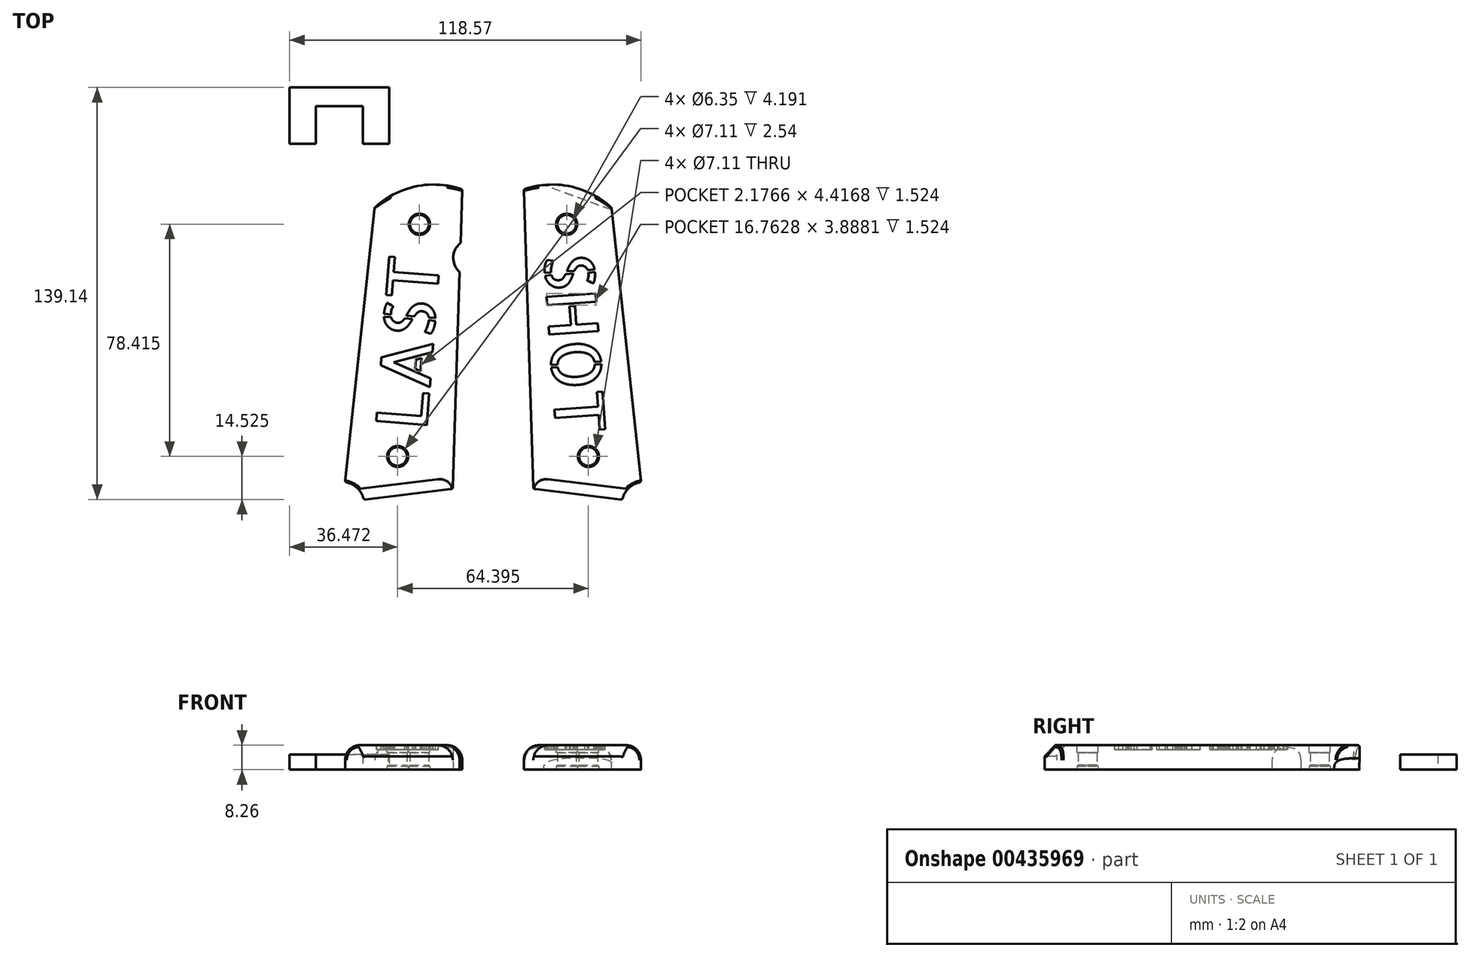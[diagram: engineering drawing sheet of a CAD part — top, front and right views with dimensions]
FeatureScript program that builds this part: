
annotation { "Feature Type Name" : "Feature", "Feature Type Description" : "" }
export const myFeature = defineFeature(function(context is Context, id is Id, definition is map)
    precondition{}
    {
        {
            var Q0;
            Q0=qCreatedBy(makeId("Top.planeOp"),FACE);
            var sketch = newSketch(context, id + "F0", { "sketchPlane" : qUnion([Q0])});
            skLineSegment(sketch, "E0", {"start": v(-13.61, -63.5) * mm, "end": v(-43.66, -67.13) * mm});
            skArc(sketch, "E1", {"start": v(-10.4, 37.63) * mm, "mid": v(-26.05, 38.66) * mm, "end": v(-39.98, 31.44) * mm});
            skArc(sketch, "E2", {"start": v(-10.97, 19.52) * mm, "mid": v(-13.43, 14.7) * mm, "end": v(-11.28, 9.73) * mm});
            skLineSegment(sketch, "E3", {"start": v(-10.4, 37.63) * mm, "end": v(-10.97, 19.52) * mm});
            skLineSegment(sketch, "E4", {"start": v(-11.28, 9.73) * mm, "end": v(-13.61, -63.5) * mm});
            skCircle(sketch, "E5", {"center": v(-32.2, -52.55) * mm, "radius": 3.18 * mm});
            skCircle(sketch, "E6", {"center": v(-24.84, 25.87) * mm, "radius": 3.18 * mm});
            skArc(sketch, "E7", {"start": v(-43.66, -67.13) * mm, "mid": v(-45.85, -63.16) * mm, "end": v(-49.96, -61.24) * mm});
            skLineSegment(sketch, "E8.trimOffspring", {"start": v(-49.96, -61.24) * mm, "end": v(-39.98, 31.44) * mm});
            skPoint(sketch, "E9.orphan", {"position": v(-51.52, -68.08) * mm});
            skPoint(sketch, "E10.MirrorP", {"position": v(51.52, -68.08) * mm});
            skCircle(sketch, "E11.MirrorC", {"center": v(24.84, 25.87) * mm, "radius": 3.18 * mm});
            skCircle(sketch, "E12.MirrorC", {"center": v(32.2, -52.55) * mm, "radius": 3.18 * mm});
            skLineSegment(sketch, "E13.MirrorCS", {"start": v(11.28, 9.73) * mm, "end": v(13.61, -63.5) * mm});
            skLineSegment(sketch, "E14.MirrorCS", {"start": v(10.4, 37.63) * mm, "end": v(10.97, 19.52) * mm});
            skLineSegment(sketch, "E15.MirrorCS", {"start": v(49.96, -61.24) * mm, "end": v(39.98, 31.44) * mm});
            skArc(sketch, "E16.MirrorCS", {"start": v(43.66, -67.13) * mm, "mid": v(45.85, -63.16) * mm, "end": v(49.96, -61.24) * mm});
            skLineSegment(sketch, "E17.MirrorCS", {"start": v(13.61, -63.5) * mm, "end": v(43.66, -67.13) * mm});
            skArc(sketch, "E18.MirrorCS", {"start": v(10.4, 37.63) * mm, "mid": v(26.05, 38.66) * mm, "end": v(39.98, 31.44) * mm});
            skLineSegment(sketch, "E19", {"start": v(10.97, 19.52) * mm, "end": v(11.28, 9.73) * mm});
            skSolve(sketch);
        }
        {
            var Q0;
            Q0 = qSketchRegion(id + "F0", true);
            extrude(context, id + "F1", {"entities" : qUnion([Q0]), "depth" : 8.25 * mm});
        }
        {
            var Q0;
            Q0=qCreatedBy(makeId("Top.planeOp"),FACE);
            var sketch = newSketch(context, id + "F2", { "sketchPlane" : qUnion([Q0])});
            skLineSegment(sketch, "E20", {"start": v(-59.78, 65.72) * mm, "end": v(-43.9, 65.72) * mm});
            skLineSegment(sketch, "E21", {"start": v(-43.9, 65.72) * mm, "end": v(-43.9, 53.02) * mm});
            skLineSegment(sketch, "E22", {"start": v(-43.9, 53.02) * mm, "end": v(-35.01, 53.02) * mm});
            skLineSegment(sketch, "E23", {"start": v(-35.01, 53.02) * mm, "end": v(-35.01, 72.07) * mm});
            skLineSegment(sketch, "E24", {"start": v(-35.01, 72.07) * mm, "end": v(-68.67, 72.07) * mm});
            skLineSegment(sketch, "E25", {"start": v(-68.67, 72.07) * mm, "end": v(-68.67, 53.02) * mm});
            skLineSegment(sketch, "E26", {"start": v(-68.67, 53.02) * mm, "end": v(-59.78, 53.02) * mm});
            skLineSegment(sketch, "E27", {"start": v(-59.78, 53.02) * mm, "end": v(-59.78, 65.72) * mm});
            skSolve(sketch);
        }
        {
            var Q0;
            Q0 = qSketchRegion(id + "F2", true);
            extrude(context, id + "F3", {"entities" : qUnion([Q0]), "depth" : 5.08 * mm});
        }
        {
            var Q0;
            Q0=qCreatedBy(makeId("Front.planeOp"),FACE);
            var sketch = newSketch(context, id + "F4", { "sketchPlane" : qUnion([Q0])});
            skLineSegment(sketch, "E28", {"start": v(0, 75.66) * mm, "end": v(0, -56.7) * mm});
            skSolve(sketch);
        }
        {
            var Q0;
            Q0=sQuery(id+"F4.wireOp",EDGE,"E28");
            cPlane(context, id + "F5", {"entities" : qUnion([Q0]), "cplaneType" : CPlaneType.LINE_ANGLE, "offset" : 25.4 * mm, "angle" : 20 * degree, "width" : 152.4 * mm, "height" : 152.4 * mm});
        }
        {
            var Q0;
            Q0=qCreatedBy(id+"F5.planeOp",FACE);
            var sketch = newSketch(context, id + "F6", { "sketchPlane" : qUnion([Q0])});
            skCircle(sketch, "E29", {"center": v(-45.72, 0.67) * mm, "radius": 3.18 * mm});
            skSolve(sketch);
        }
        {
            var Q0;
            Q0 = qSketchRegion(id + "F6", true);
            extrude(context, id + "F7", {"entities" : qUnion([Q0]), "operationType" : NewBodyOperationType.REMOVE, "oppositeDirection" : true, "depth" : 38.1 * mm});
        }
        {
            var Q0;
            Q0=makeQuery(id+"F1.opExtrude","CAP_EDGE",EDGE,{"disambiguationData":[OSD([sQuery(id+"F0.wireOp",EDGE,"a4e4d398-114f-4659-ac55-d26a9042ed512.MirrorCS")])],"isStart":false});
            var Q1;
            Q1=makeQuery(id+"F1.opExtrude","CAP_EDGE",EDGE,{"disambiguationData":[OSD([sQuery(id+"F0.wireOp",EDGE,"fEtNWjUg-NbEW-A6zS-67Gl-Nols5Lw7AtEy")])],"isStart":false});
            var Q2;
            Q2=makeQuery(id+"F1.opExtrude","CAP_EDGE",EDGE,{"disambiguationData":[OSD([sQuery(id+"F0.wireOp",EDGE,"E4")])],"isStart":false});
            var Q3;
            Q3=makeQuery(id+"F1.opExtrude","CAP_EDGE",EDGE,{"disambiguationData":[OSD([sQuery(id+"F0.wireOp",EDGE,"a4e4d398-114f-4659-ac55-d26a9042ed510.MirrorCS")])],"isStart":false});
            fillet(context, id + "F8", {"entities" : qUnion([Q0, Q1, Q2, Q3]), "radius" : 5.08 * mm, "tangentPropagation" : true, "allowEdgeOverflow" : false});
        }
        {
            var Q0;
            Q0=makeQuery(id+"F1.opExtrude","CAP_EDGE",EDGE,{"disambiguationData":[OSD([sQuery(id+"F0.wireOp",EDGE,"E13.MirrorCS"),sQuery(id+"F0.wireOp",EDGE,"E14.MirrorCS"),sQuery(id+"F0.wireOp",EDGE,"E19")])],"isStart":false});
            var Q1;
            Q1=makeQuery(id+"F1.opExtrude","CAP_EDGE",EDGE,{"disambiguationData":[OSD([sQuery(id+"F0.wireOp",EDGE,"E15.MirrorCS")])],"isStart":false});
            var Q2;
            Q2=makeQuery(id+"F1.opExtrude","CAP_EDGE",EDGE,{"disambiguationData":[OSD([sQuery(id+"F0.wireOp",EDGE,"E8.trimOffspring")])],"isStart":false});
            fillet(context, id + "F9", {"entities" : qUnion([Q0, Q1, Q2]), "radius" : 5.08 * mm, "tangentPropagation" : true, "allowEdgeOverflow" : false});
        }
        {
            var Q0;
            Q0=makeQuery(id+"F1.opExtrude","CAP_EDGE",EDGE,{"disambiguationData":[OSD([sQuery(id+"F0.wireOp",EDGE,"E0")])],"isStart":false});
            var Q1;
            Q1=makeQuery(id+"F1.opExtrude","CAP_EDGE",EDGE,{"disambiguationData":[OSD([sQuery(id+"F0.wireOp",EDGE,"E17.MirrorCS")])],"isStart":false});
            chamfer(context, id + "F10", {"entities" : qUnion([Q0, Q1]), "width" : 3.8 * mm});
        }
        {
            var Q0;
            Q0=makeQuery(id+"F1.opExtrude","CAP_EDGE",EDGE,{"disambiguationData":[OSD([sQuery(id+"F0.wireOp",EDGE,"E18.MirrorCS")])],"isStart":false});
            var Q1;
            Q1=makeQuery(id+"F9.opFillet","BLEND_EDGE",EDGE,{"blendedFrom":[makeQuery(id+"F1.opExtrude","CAP_EDGE",EDGE,{"disambiguationData":[OSD([sQuery(id+"F0.wireOp",EDGE,"E13.MirrorCS"),sQuery(id+"F0.wireOp",EDGE,"E14.MirrorCS"),sQuery(id+"F0.wireOp",EDGE,"E19")])],"isStart":false}),makeQuery(id+"F1.opExtrude","SWEPT_FACE",FACE,{"disambiguationData":[OSD([sQuery(id+"F0.wireOp",EDGE,"E18.MirrorCS")])]})],"blendedInto":[makeQuery(id+"F1.opExtrude","SWEPT_FACE",FACE,{"disambiguationData":[OSD([sQuery(id+"F0.wireOp",EDGE,"E18.MirrorCS")])]})]});
            var Q2;
            Q2=makeQuery(id+"F1.opExtrude","SWEPT_EDGE",EDGE,{"disambiguationData":[OSD([sQuery(id+"F0.wireOp",EDGE,"E14.MirrorCS"),sQuery(id+"F0.wireOp",EDGE,"E18.MirrorCS")])]});
            var Q3;
            Q3=makeQuery(id+"F9.opFillet","BLEND_EDGE",EDGE,{"blendedFrom":[makeQuery(id+"F1.opExtrude","CAP_EDGE",EDGE,{"disambiguationData":[OSD([sQuery(id+"F0.wireOp",EDGE,"E15.MirrorCS")])],"isStart":false}),makeQuery(id+"F1.opExtrude","SWEPT_FACE",FACE,{"disambiguationData":[OSD([sQuery(id+"F0.wireOp",EDGE,"E18.MirrorCS")])]})],"blendedInto":[makeQuery(id+"F1.opExtrude","SWEPT_FACE",FACE,{"disambiguationData":[OSD([sQuery(id+"F0.wireOp",EDGE,"E18.MirrorCS")])]})]});
            var Q4;
            Q4=makeQuery(id+"F1.opExtrude","SWEPT_EDGE",EDGE,{"disambiguationData":[OSD([sQuery(id+"F0.wireOp",EDGE,"E1"),sQuery(id+"F0.wireOp",EDGE,"E3")])]});
            var Q5;
            Q5=makeQuery(id+"F8.opFillet","BLEND_EDGE",EDGE,{"blendedFrom":[makeQuery(id+"F1.opExtrude","CAP_EDGE",EDGE,{"disambiguationData":[OSD([sQuery(id+"F0.wireOp",EDGE,"E4")])],"isStart":false}),makeQuery(id+"F1.opExtrude","SWEPT_FACE",FACE,{"disambiguationData":[OSD([sQuery(id+"F0.wireOp",EDGE,"E1")])]})],"blendedInto":[makeQuery(id+"F1.opExtrude","SWEPT_FACE",FACE,{"disambiguationData":[OSD([sQuery(id+"F0.wireOp",EDGE,"E1")])]})]});
            var Q6;
            Q6=makeQuery(id+"F1.opExtrude","CAP_EDGE",EDGE,{"disambiguationData":[OSD([sQuery(id+"F0.wireOp",EDGE,"E1")])],"isStart":false});
            var Q7;
            Q7=makeQuery(id+"F9.opFillet","BLEND_EDGE",EDGE,{"blendedFrom":[makeQuery(id+"F1.opExtrude","CAP_EDGE",EDGE,{"disambiguationData":[OSD([sQuery(id+"F0.wireOp",EDGE,"E8.trimOffspring")])],"isStart":false}),makeQuery(id+"F1.opExtrude","SWEPT_FACE",FACE,{"disambiguationData":[OSD([sQuery(id+"F0.wireOp",EDGE,"E1")])]})],"blendedInto":[makeQuery(id+"F1.opExtrude","SWEPT_FACE",FACE,{"disambiguationData":[OSD([sQuery(id+"F0.wireOp",EDGE,"E1")])]})]});
            var Q8;
            Q8=makeQuery(id+"F1.opExtrude","SWEPT_EDGE",EDGE,{"disambiguationData":[OSD([sQuery(id+"F0.wireOp",EDGE,"E0"),sQuery(id+"F0.wireOp",EDGE,"E4")])]});
            var Q9;
            Q9=makeQuery(id+"F8.opFillet","BLEND_EDGE",EDGE,{"blendedFrom":[makeQuery(id+"F1.opExtrude","CAP_EDGE",EDGE,{"disambiguationData":[OSD([sQuery(id+"F0.wireOp",EDGE,"E4")])],"isStart":false}),makeQuery(id+"F1.opExtrude","SWEPT_FACE",FACE,{"disambiguationData":[OSD([sQuery(id+"F0.wireOp",EDGE,"E0")])]})],"blendedInto":[makeQuery(id+"F1.opExtrude","SWEPT_FACE",FACE,{"disambiguationData":[OSD([sQuery(id+"F0.wireOp",EDGE,"E0")])]})]});
            var Q10;
            Q10=makeQuery(id+"F1.opExtrude","SWEPT_EDGE",EDGE,{"disambiguationData":[OSD([sQuery(id+"F0.wireOp",EDGE,"E0"),sQuery(id+"F0.wireOp",EDGE,"E7")])]});
            var Q11;
            Q11=makeQuery(id+"F10.opChamfer","BLEND_EDGE",EDGE,{"blendedFrom":[makeQuery(id+"F1.opExtrude","CAP_EDGE",EDGE,{"disambiguationData":[OSD([sQuery(id+"F0.wireOp",EDGE,"E0")])],"isStart":false}),makeQuery(id+"F1.opExtrude","SWEPT_FACE",FACE,{"disambiguationData":[OSD([sQuery(id+"F0.wireOp",EDGE,"E7")])]})],"blendedInto":[makeQuery(id+"F1.opExtrude","SWEPT_FACE",FACE,{"disambiguationData":[OSD([sQuery(id+"F0.wireOp",EDGE,"E7")])]})]});
            var Q12;
            Q12=makeQuery(id+"F1.opExtrude","SWEPT_EDGE",EDGE,{"disambiguationData":[OSD([sQuery(id+"F0.wireOp",EDGE,"E7"),sQuery(id+"F0.wireOp",EDGE,"E8.trimOffspring")])]});
            var Q13;
            Q13=makeQuery(id+"F9.opFillet","BLEND_EDGE",EDGE,{"blendedFrom":[makeQuery(id+"F1.opExtrude","CAP_EDGE",EDGE,{"disambiguationData":[OSD([sQuery(id+"F0.wireOp",EDGE,"E8.trimOffspring")])],"isStart":false}),makeQuery(id+"F1.opExtrude","SWEPT_FACE",FACE,{"disambiguationData":[OSD([sQuery(id+"F0.wireOp",EDGE,"E7")])]})],"blendedInto":[makeQuery(id+"F1.opExtrude","SWEPT_FACE",FACE,{"disambiguationData":[OSD([sQuery(id+"F0.wireOp",EDGE,"E7")])]})]});
            var Q14;
            Q14=makeQuery(id+"F1.opExtrude","CAP_EDGE",EDGE,{"disambiguationData":[OSD([sQuery(id+"F0.wireOp",EDGE,"E7")])],"isStart":false});
            var Q15;
            Q15=makeQuery(id+"F1.opExtrude","SWEPT_EDGE",EDGE,{"disambiguationData":[OSD([sQuery(id+"F0.wireOp",EDGE,"E13.MirrorCS"),sQuery(id+"F0.wireOp",EDGE,"E17.MirrorCS")])]});
            var Q16;
            Q16=makeQuery(id+"F9.opFillet","BLEND_EDGE",EDGE,{"blendedFrom":[makeQuery(id+"F1.opExtrude","CAP_EDGE",EDGE,{"disambiguationData":[OSD([sQuery(id+"F0.wireOp",EDGE,"E13.MirrorCS"),sQuery(id+"F0.wireOp",EDGE,"E14.MirrorCS"),sQuery(id+"F0.wireOp",EDGE,"E19")])],"isStart":false}),makeQuery(id+"F1.opExtrude","SWEPT_FACE",FACE,{"disambiguationData":[OSD([sQuery(id+"F0.wireOp",EDGE,"E17.MirrorCS")])]})],"blendedInto":[makeQuery(id+"F1.opExtrude","SWEPT_FACE",FACE,{"disambiguationData":[OSD([sQuery(id+"F0.wireOp",EDGE,"E17.MirrorCS")])]})]});
            var Q17;
            Q17=makeQuery(id+"F1.opExtrude","SWEPT_EDGE",EDGE,{"disambiguationData":[OSD([sQuery(id+"F0.wireOp",EDGE,"E16.MirrorCS"),sQuery(id+"F0.wireOp",EDGE,"E17.MirrorCS")])]});
            var Q18;
            Q18=makeQuery(id+"F10.opChamfer","BLEND_EDGE",EDGE,{"blendedFrom":[makeQuery(id+"F1.opExtrude","CAP_EDGE",EDGE,{"disambiguationData":[OSD([sQuery(id+"F0.wireOp",EDGE,"E17.MirrorCS")])],"isStart":false}),makeQuery(id+"F1.opExtrude","SWEPT_FACE",FACE,{"disambiguationData":[OSD([sQuery(id+"F0.wireOp",EDGE,"E16.MirrorCS")])]})],"blendedInto":[makeQuery(id+"F1.opExtrude","SWEPT_FACE",FACE,{"disambiguationData":[OSD([sQuery(id+"F0.wireOp",EDGE,"E16.MirrorCS")])]})]});
            var Q19;
            Q19=makeQuery(id+"F1.opExtrude","CAP_EDGE",EDGE,{"disambiguationData":[OSD([sQuery(id+"F0.wireOp",EDGE,"E16.MirrorCS")])],"isStart":false});
            var Q20;
            Q20=makeQuery(id+"F9.opFillet","BLEND_EDGE",EDGE,{"blendedFrom":[makeQuery(id+"F1.opExtrude","CAP_EDGE",EDGE,{"disambiguationData":[OSD([sQuery(id+"F0.wireOp",EDGE,"E15.MirrorCS")])],"isStart":false}),makeQuery(id+"F1.opExtrude","SWEPT_FACE",FACE,{"disambiguationData":[OSD([sQuery(id+"F0.wireOp",EDGE,"E16.MirrorCS")])]})],"blendedInto":[makeQuery(id+"F1.opExtrude","SWEPT_FACE",FACE,{"disambiguationData":[OSD([sQuery(id+"F0.wireOp",EDGE,"E16.MirrorCS")])]})]});
            var Q21;
            Q21=makeQuery(id+"F1.opExtrude","SWEPT_EDGE",EDGE,{"disambiguationData":[OSD([sQuery(id+"F0.wireOp",EDGE,"E15.MirrorCS"),sQuery(id+"F0.wireOp",EDGE,"E16.MirrorCS")])]});
            var Q22;
            Q22=makeQuery(id+"F1.opExtrude","SWEPT_EDGE",EDGE,{"disambiguationData":[OSD([sQuery(id+"F0.wireOp",EDGE,"E1"),sQuery(id+"F0.wireOp",EDGE,"E8.trimOffspring")])]});
            fillet(context, id + "F11", {"entities" : qUnion([Q0, Q1, Q2, Q3, Q4, Q5, Q6, Q7, Q8, Q9, Q10, Q11, Q12, Q13, Q14, Q15, Q16, Q17, Q18, Q19, Q20, Q21, Q22]), "radius" : 0.64 * mm, "tangentPropagation" : true, "allowEdgeOverflow" : false});
        }
        {
            var Q0;
            Q0=makeQuery(id+"F1.opExtrude","CAP_FACE",FACE,{"disambiguationData":[OSD([sQuery(id+"F0.wireOp",EDGE,"E11.MirrorC"),sQuery(id+"F0.wireOp",EDGE,"E12.MirrorC"),sQuery(id+"F0.wireOp",EDGE,"E13.MirrorCS"),sQuery(id+"F0.wireOp",EDGE,"E14.MirrorCS"),sQuery(id+"F0.wireOp",EDGE,"E15.MirrorCS"),sQuery(id+"F0.wireOp",EDGE,"E16.MirrorCS"),sQuery(id+"F0.wireOp",EDGE,"E17.MirrorCS"),sQuery(id+"F0.wireOp",EDGE,"E18.MirrorCS"),sQuery(id+"F0.wireOp",EDGE,"E19")])],"isStart":false});
            var sketch = newSketch(context, id + "F12", { "sketchPlane" : qUnion([Q0])});
            skText(sketch, "E30", { "text": "SHOT", "fontName": "AllertaStencil-Regular.ttf"});
            const initialGuessF12  = {"E30": [0.01709, 0.0156, 0.069, -0.99762, 0.01662]};
            skSetInitialGuess(sketch, initialGuessF12);
            skSolve(sketch);
        }
        {
            var Q0;
            Q0 = qSketchRegion(id + "F12", true);
            extrude(context, id + "F13", {"entities" : qUnion([Q0]), "operationType" : NewBodyOperationType.REMOVE, "oppositeDirection" : true, "depth" : 1.52 * mm});
        }
        {
            var Q0;
            Q0=makeQuery(id+"F1.opExtrude","CAP_FACE",FACE,{"disambiguationData":[OSD([sQuery(id+"F0.wireOp",EDGE,"E0"),sQuery(id+"F0.wireOp",EDGE,"E1"),sQuery(id+"F0.wireOp",EDGE,"E2"),sQuery(id+"F0.wireOp",EDGE,"E3"),sQuery(id+"F0.wireOp",EDGE,"E4"),sQuery(id+"F0.wireOp",EDGE,"E5"),sQuery(id+"F0.wireOp",EDGE,"E6"),sQuery(id+"F0.wireOp",EDGE,"E7"),sQuery(id+"F0.wireOp",EDGE,"E8.trimOffspring")])],"isStart":false});
            var sketch = newSketch(context, id + "F14", { "sketchPlane" : qUnion([Q0])});
            skText(sketch, "E31", { "text": "LAST", "fontName": "AllertaStencil-Regular.ttf"});
            const initialGuessF14  = {"E31": [-0.02256, -0.0441, 0.07965, 0.99682, 0.0171]};
            skSetInitialGuess(sketch, initialGuessF14);
            skSolve(sketch);
        }
        {
            var Q0;
            Q0 = qSketchRegion(id + "F14", true);
            extrude(context, id + "F15", {"entities" : qUnion([Q0]), "operationType" : NewBodyOperationType.REMOVE, "oppositeDirection" : true, "depth" : 1.52 * mm});
        }
        {
            var Q0;
            Q0=makeQuery(id+"F1.opExtrude","CAP_FACE",FACE,{"disambiguationData":[OSD([sQuery(id+"F0.wireOp",EDGE,"E11.MirrorC"),sQuery(id+"F0.wireOp",EDGE,"E12.MirrorC"),sQuery(id+"F0.wireOp",EDGE,"E13.MirrorCS"),sQuery(id+"F0.wireOp",EDGE,"E14.MirrorCS"),sQuery(id+"F0.wireOp",EDGE,"E15.MirrorCS"),sQuery(id+"F0.wireOp",EDGE,"E16.MirrorCS"),sQuery(id+"F0.wireOp",EDGE,"E17.MirrorCS"),sQuery(id+"F0.wireOp",EDGE,"E18.MirrorCS"),sQuery(id+"F0.wireOp",EDGE,"E19")])],"isStart":false});
            var sketch = newSketch(context, id + "F16", { "sketchPlane" : qUnion([Q0])});
            skCircle(sketch, "E32", {"center": v(24.84, 25.87) * mm, "radius": 3.56 * mm});
            skCircle(sketch, "E33", {"center": v(32.2, -52.55) * mm, "radius": 3.56 * mm});
            skSolve(sketch);
        }
        {
            var Q0;
            Q0 = qSketchRegion(id + "F16", true);
            extrude(context, id + "F17", {"entities" : qUnion([Q0]), "operationType" : NewBodyOperationType.REMOVE, "oppositeDirection" : true, "depth" : 2.54 * mm});
        }
        {
            var Q0;
            Q0=makeQuery(id+"F1.opExtrude","CAP_FACE",FACE,{"disambiguationData":[OSD([sQuery(id+"F0.wireOp",EDGE,"E0"),sQuery(id+"F0.wireOp",EDGE,"E1"),sQuery(id+"F0.wireOp",EDGE,"E2"),sQuery(id+"F0.wireOp",EDGE,"E3"),sQuery(id+"F0.wireOp",EDGE,"E4"),sQuery(id+"F0.wireOp",EDGE,"E5"),sQuery(id+"F0.wireOp",EDGE,"E6"),sQuery(id+"F0.wireOp",EDGE,"E7"),sQuery(id+"F0.wireOp",EDGE,"E8.trimOffspring")])],"isStart":false});
            var sketch = newSketch(context, id + "F18", { "sketchPlane" : qUnion([Q0])});
            skCircle(sketch, "E34", {"center": v(-24.84, 25.87) * mm, "radius": 3.56 * mm});
            skCircle(sketch, "E35", {"center": v(-32.2, -52.55) * mm, "radius": 3.56 * mm});
            skSolve(sketch);
        }
        {
            var Q0;
            Q0 = qSketchRegion(id + "F18", true);
            extrude(context, id + "F19", {"entities" : qUnion([Q0]), "operationType" : NewBodyOperationType.REMOVE, "oppositeDirection" : true, "depth" : 2.54 * mm});
        }
        {
            var Q0;
            Q0=makeQuery(id+"F1.opExtrude","CAP_FACE",FACE,{"disambiguationData":[OSD([sQuery(id+"F0.wireOp",EDGE,"E11.MirrorC"),sQuery(id+"F0.wireOp",EDGE,"E12.MirrorC"),sQuery(id+"F0.wireOp",EDGE,"E13.MirrorCS"),sQuery(id+"F0.wireOp",EDGE,"E14.MirrorCS"),sQuery(id+"F0.wireOp",EDGE,"E15.MirrorCS"),sQuery(id+"F0.wireOp",EDGE,"E16.MirrorCS"),sQuery(id+"F0.wireOp",EDGE,"E17.MirrorCS"),sQuery(id+"F0.wireOp",EDGE,"E18.MirrorCS"),sQuery(id+"F0.wireOp",EDGE,"E19")])],"isStart":true});
            var sketch = newSketch(context, id + "F20", { "sketchPlane" : qUnion([Q0])});
            skCircle(sketch, "E36", {"center": v(32.2, 52.55) * mm, "radius": 3.56 * mm});
            skCircle(sketch, "E37", {"center": v(24.84, -25.87) * mm, "radius": 3.56 * mm});
            skSolve(sketch);
        }
        {
            var Q0;
            Q0 = qSketchRegion(id + "F20", true);
            extrude(context, id + "F21", {"entities" : qUnion([Q0]), "operationType" : NewBodyOperationType.REMOVE, "oppositeDirection" : true, "depth" : 1.52 * mm});
        }
        {
            var Q0;
            Q0=makeQuery(id+"F1.opExtrude","CAP_FACE",FACE,{"disambiguationData":[OSD([sQuery(id+"F0.wireOp",EDGE,"E0"),sQuery(id+"F0.wireOp",EDGE,"E1"),sQuery(id+"F0.wireOp",EDGE,"E2"),sQuery(id+"F0.wireOp",EDGE,"E3"),sQuery(id+"F0.wireOp",EDGE,"E4"),sQuery(id+"F0.wireOp",EDGE,"E5"),sQuery(id+"F0.wireOp",EDGE,"E6"),sQuery(id+"F0.wireOp",EDGE,"E7"),sQuery(id+"F0.wireOp",EDGE,"E8.trimOffspring")])],"isStart":true});
            var sketch = newSketch(context, id + "F22", { "sketchPlane" : qUnion([Q0])});
            skCircle(sketch, "E38", {"center": v(-24.84, -25.87) * mm, "radius": 3.56 * mm});
            skCircle(sketch, "E39", {"center": v(-32.2, 52.55) * mm, "radius": 3.56 * mm});
            skSolve(sketch);
        }
        {
            var Q0;
            Q0 = qSketchRegion(id + "F22", true);
            extrude(context, id + "F23", {"entities" : qUnion([Q0]), "operationType" : NewBodyOperationType.REMOVE, "oppositeDirection" : true, "depth" : 1.52 * mm});
        }
        {
            var Q0;
            Q0=makeQuery(id+"F23.boolean.opBoolean","COPY",EDGE,{"derivedFrom":makeQuery(id+"F23.opExtrude","CAP_EDGE",EDGE,{"disambiguationData":[OSD([sQuery(id+"F22.wireOp",EDGE,"E39")])],"isStart":false})});
            var Q1;
            Q1=makeQuery(id+"F21.boolean.opBoolean","COPY",EDGE,{"derivedFrom":makeQuery(id+"F21.opExtrude","CAP_EDGE",EDGE,{"disambiguationData":[OSD([sQuery(id+"F20.wireOp",EDGE,"E36")])],"isStart":false})});
            var Q2;
            Q2=makeQuery(id+"F21.boolean.opBoolean","COPY",EDGE,{"derivedFrom":makeQuery(id+"F21.opExtrude","CAP_EDGE",EDGE,{"disambiguationData":[OSD([sQuery(id+"F20.wireOp",EDGE,"E37")])],"isStart":false})});
            var Q3;
            Q3=makeQuery(id+"F23.boolean.opBoolean","COPY",EDGE,{"derivedFrom":makeQuery(id+"F23.opExtrude","CAP_EDGE",EDGE,{"disambiguationData":[OSD([sQuery(id+"F22.wireOp",EDGE,"E38")])],"isStart":false})});
            chamfer(context, id + "F24", {"entities" : qUnion([Q0, Q1, Q2, Q3]), "width" : 0.38 * mm, "tangentPropagation" : true});
        }
    });
